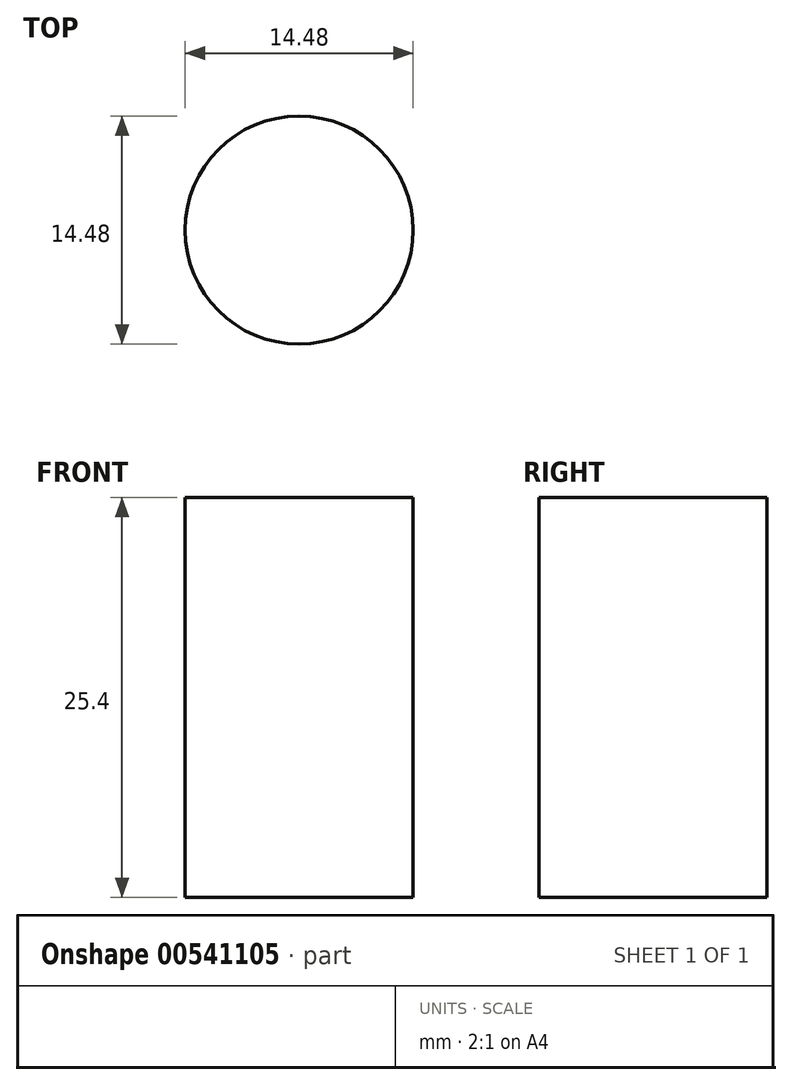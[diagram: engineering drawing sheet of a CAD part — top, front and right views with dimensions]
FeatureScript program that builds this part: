
annotation { "Feature Type Name" : "Feature", "Feature Type Description" : "" }
export const myFeature = defineFeature(function(context is Context, id is Id, definition is map)
    precondition{}
    {
        {
            var Q0;
            Q0=qCreatedBy(makeId("Top.planeOp"),FACE);
            var sketch = newSketch(context, id + "F0", { "sketchPlane" : qUnion([Q0])});
            skCircle(sketch, "E0", {"center": v(-7.84, 12.68) * mm, "radius": 7.24 * mm});
            skSolve(sketch);
        }
        {
            var Q0;
            Q0=makeQuery(id+"F0.imprint","IMPRINT",FACE,{"disambiguationData":[TD([[makeQuery(id+"F0.imprint","IMPRINT",EDGE,{"derivedFrom":sQuery(id+"F0.wireOp",EDGE,"E0")}),1.0]])]});
            extrude(context, id + "F1", {"entities" : qUnion([Q0]), "depth" : 25.4 * mm, "offsetDistance" : 25.4 * mm});
        }
    });
